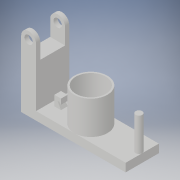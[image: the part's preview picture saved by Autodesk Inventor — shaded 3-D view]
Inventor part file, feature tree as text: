
AUTODESK INVENTOR PART (.ipt)
format: ipt  version: 2019 (Build 230136000, 136)  size: 177,152 bytes
history: native  units: in
note: dims shown in document units (in); Inventor stores cm internally (conversion verified against a paired STEP export)
features: sketch x8, extrude x6
ambient origin geometry x8: Origin, YZ Plane, XZ Plane, XY Plane, X Axis, Y Axis, Z Axis, Center Point
bodies: Solid1 (feature_tree)
feature tree (14):
  extrude  "Extrusion1"  Depth=0.1969in
  sketch  "Sketch2"  dims[d6=0.1772in d7=0.1969in]
  sketch  "Sketch6"  dims[d8=0.3543in d9=2.126in]
  extrude  "Extrusion5"  Depth=0.1969in
  sketch  "Sketch8"  dims[d13=0.2559in d14=0.7874in]
  extrude  "Extrusion6"  Depth=2.126in
  extrude  "Extrusion7"  Depth=0.1181in
  extrude  "Extrusion8"  Depth=0.7874in
  extrude  "Extrusion9"  Depth=0.3937in
  sketch  "Sketch1"  dims[d0=1.5748in d2=0.1969in]
  sketch  "Sketch7"  dims[d10=0.7874in d11=0.0in d12=0.1181in]
  sketch  "Sketch9"  dims[d16=0.9055in d19=0.3937in]
  sketch  "Sketch10"  dims[d20=0.1575in]
  sketch  "Sketch11"  dims[d21=0.3937in d22=0.6693in d40=0.5512in d41=0.5512in d42=0.5906in d43=0.5512in d44=0.0in d47=1.2795in d48=0.7874in d49=0.0in d50=0.7087in d51=0.9843in d52=0.0in d53=0.1575in d54=0.1575in d55=0.315in d56=0.1181in d57=0.2362in d58=0.0in d59=0.0787in d60=0.0394in d61=0.1496in d62=0.1102in d63=0.1575in d64=0.0in]
